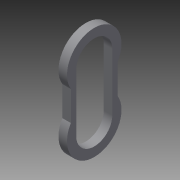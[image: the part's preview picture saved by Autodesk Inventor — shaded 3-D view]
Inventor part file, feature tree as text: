
AUTODESK INVENTOR PART (.ipt)
format: ipt  version: 2015 (Build 190159000, 159)  size: 87,040 bytes
history: native  units: mm
features: extrude x1, sketch x1
ambient origin geometry x8: Origin, YZ Plane, XZ Plane, XY Plane, X Axis, Y Axis, Z Axis, Center Point
bodies: Solid1 (feature_tree)
feature tree (2):
  extrude  "Extrusion1"  Depth=17.0mm
  sketch  "Sketch1"  dims[d12=17.0mm d13=17.0mm d14=4.0mm d15=0.0mm]
